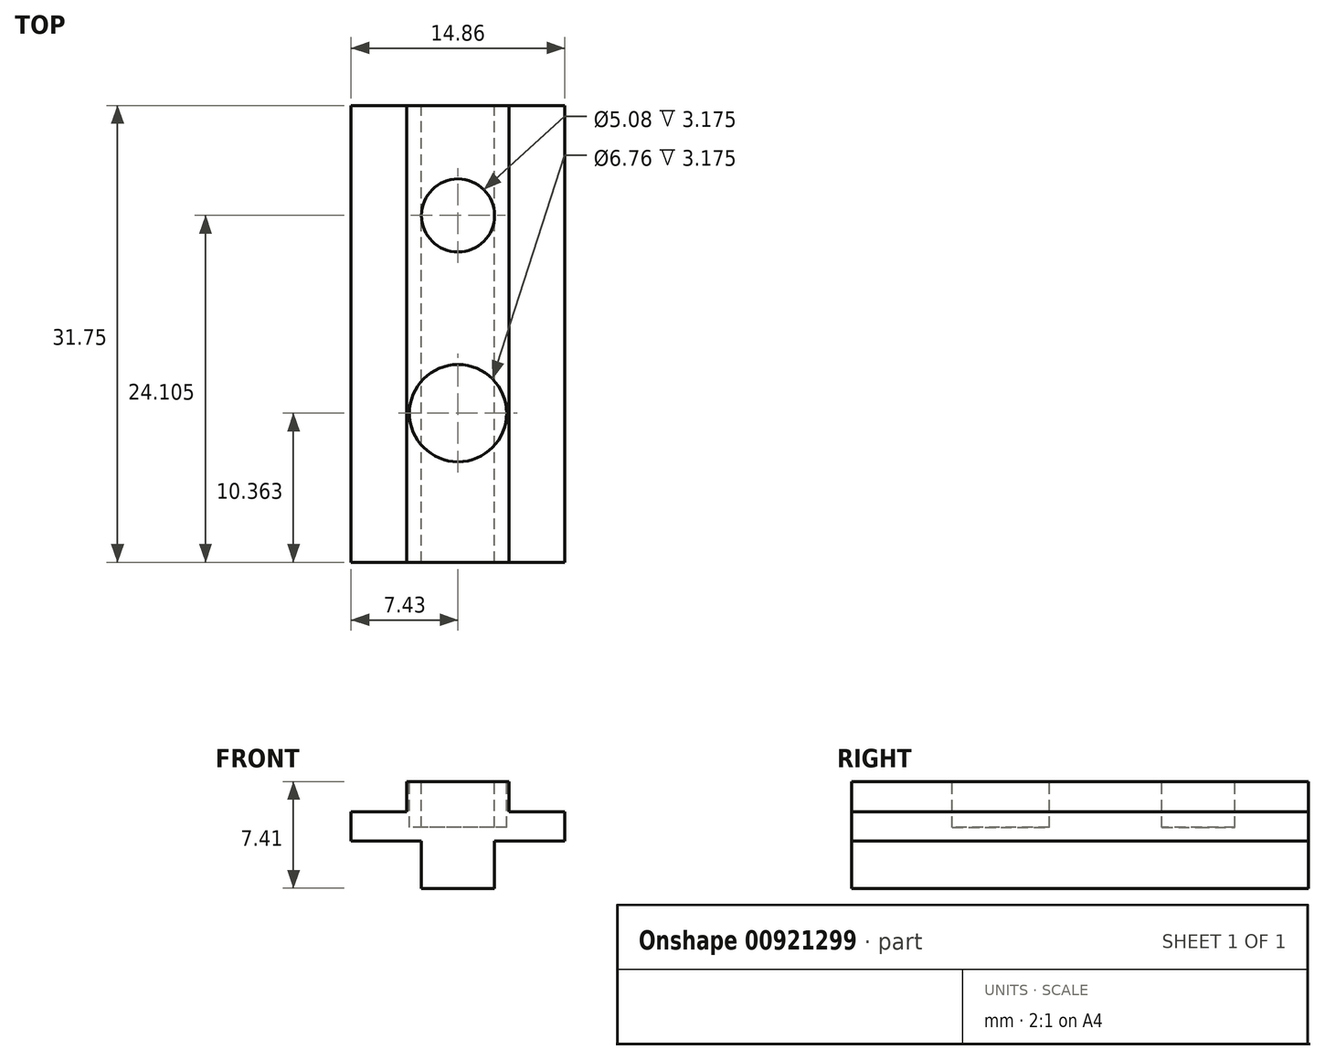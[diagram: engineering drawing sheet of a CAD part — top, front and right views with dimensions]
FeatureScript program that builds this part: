
annotation { "Feature Type Name" : "Feature", "Feature Type Description" : "" }
export const myFeature = defineFeature(function(context is Context, id is Id, definition is map)
    precondition{}
    {
        {
            var Q0;
            Q0=qCreatedBy(makeId("Front.planeOp"),FACE);
            var sketch = newSketch(context, id + "F0", { "sketchPlane" : qUnion([Q0])});
            skLineSegment(sketch, "E0.bottom", {"start": v(-3.56, 2.08) * mm, "end": v(3.56, 2.08) * mm});
            skLineSegment(sketch, "E0.left", {"start": v(-3.56, 2.08) * mm, "end": v(-3.56, 0) * mm});
            skLineSegment(sketch, "E0.right", {"start": v(3.56, 2.08) * mm, "end": v(3.56, 0) * mm});
            skLineSegment(sketch, "E1.bottom", {"start": v(-7.43, 0) * mm, "end": v(-3.56, 0) * mm});
            skLineSegment(sketch, "E1.top", {"start": v(-7.43, -2.03) * mm, "end": v(-2.54, -2.03) * mm});
            skLineSegment(sketch, "E1.left", {"start": v(-7.43, 0) * mm, "end": v(-7.43, -2.03) * mm});
            skLineSegment(sketch, "E1.right", {"start": v(7.43, 0) * mm, "end": v(7.43, -2.03) * mm});
            skLineSegment(sketch, "E2.top", {"start": v(-2.54, -5.33) * mm, "end": v(2.54, -5.33) * mm});
            skLineSegment(sketch, "E2.left", {"start": v(-2.54, -2.03) * mm, "end": v(-2.54, -5.33) * mm});
            skLineSegment(sketch, "E2.right", {"start": v(2.54, -2.03) * mm, "end": v(2.54, -5.33) * mm});
            skLineSegment(sketch, "E3.trimOffspring", {"start": v(3.56, 0) * mm, "end": v(7.43, 0) * mm});
            skLineSegment(sketch, "E4.trimOffspring", {"start": v(2.54, -2.03) * mm, "end": v(7.43, -2.03) * mm});
            skSolve(sketch);
        }
        {
            var Q0;
            Q0=makeQuery(id+"F0.imprint","IMPRINT",FACE,{"disambiguationData":[TD([[makeQuery(id+"F0.imprint","IMPRINT",EDGE,{"derivedFrom":sQuery(id+"F0.wireOp",EDGE,"E0.bottom")}),-1.0]])]});
            var Q1;
            {var subQ0=sQuery(id+"F0.wireOp",EDGE,"E1.left");Q1=makeQuery(id+"F0.imprint","IMPRINT",FACE,{"disambiguationData":[TD([[makeQuery(id+"F0.imprint","IMPRINT",EDGE,{"derivedFrom":subQ0}),1.0]])]});}
            var Q2;
            Q2=makeQuery(id+"F0.imprint","IMPRINT",FACE,{"disambiguationData":[TD([[makeQuery(id+"F0.imprint","IMPRINT",EDGE,{"derivedFrom":sQuery(id+"F0.wireOp",EDGE,"E2.bottom")}),-1.0]])]});
            extrude(context, id + "F1", {"entities" : qUnion([Q0, Q1, Q2]), "depth" : 31.75 * mm, "offsetDistance" : 25.4 * mm});
        }
        {
            var Q0;
            Q0=makeQuery(id+"F1.opExtrude","SWEPT_FACE",FACE,{"disambiguationData":[OSD([sQuery(id+"F0.wireOp",EDGE,"E0.bottom")])]});
            var sketch = newSketch(context, id + "F2", { "sketchPlane" : qUnion([Q0])});
            skCircle(sketch, "E5", {"center": v(0, -21.39) * mm, "radius": 3.38 * mm});
            skCircle(sketch, "E6", {"center": v(0, -7.65) * mm, "radius": 2.54 * mm});
            skPoint(sketch, "E6.centerSnap0", {"position": v(0, 0) * mm});
            skSolve(sketch);
        }
        {
            var Q0;
            Q0=makeQuery(id+"F2.imprint","IMPRINT",FACE,{"disambiguationData":[TD([[makeQuery(id+"F2.imprint","IMPRINT",EDGE,{"derivedFrom":sQuery(id+"F2.wireOp",EDGE,"fXK3Fjaw-o3fJ-Wdds-udlc-ZsNGpqsiUqFL")}),1.0]])]});
            var Q1;
            Q1=makeQuery(id+"F2.imprint","IMPRINT",FACE,{"disambiguationData":[TD([[makeQuery(id+"F2.imprint","IMPRINT",EDGE,{"derivedFrom":sQuery(id+"F2.wireOp",EDGE,"E5")}),1.0]])]});
            var Q2;
            Q2=makeQuery(id+"F2.imprint","IMPRINT",FACE,{"disambiguationData":[TD([[makeQuery(id+"F2.imprint","IMPRINT",EDGE,{"derivedFrom":sQuery(id+"F2.wireOp",EDGE,"E6")}),1.0]])]});
            extrude(context, id + "F3", {"entities" : qUnion([Q0, Q1, Q2]), "operationType" : NewBodyOperationType.REMOVE, "oppositeDirection" : true, "depth" : 3.17 * mm, "offsetDistance" : 25.4 * mm});
        }
    });
